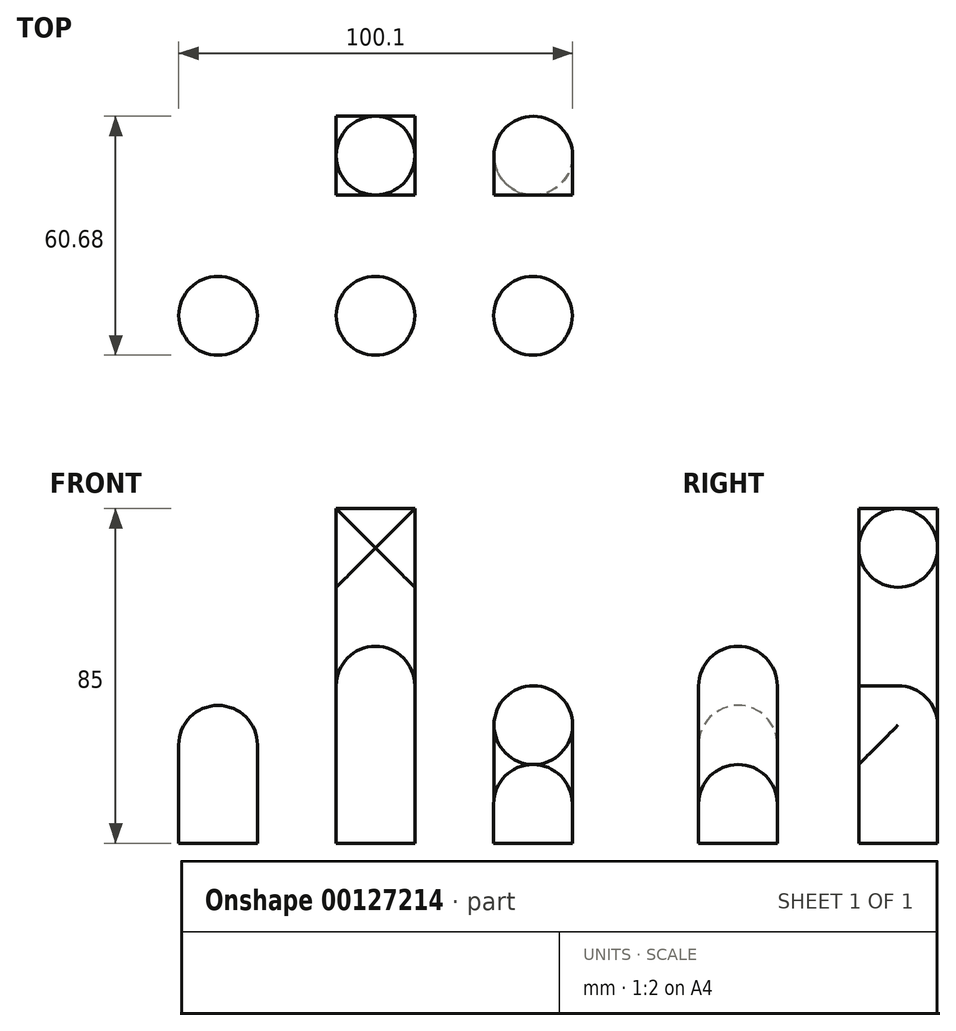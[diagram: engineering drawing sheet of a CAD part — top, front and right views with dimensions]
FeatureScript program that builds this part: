
annotation { "Feature Type Name" : "Feature", "Feature Type Description" : "" }
export const myFeature = defineFeature(function(context is Context, id is Id, definition is map)
    precondition{}
    {
        {
            var Q0;
            Q0=qCreatedBy(makeId("Top.planeOp"),FACE);
            var sketch = newSketch(context, id + "F0", { "sketchPlane" : qUnion([Q0])});
            skCircle(sketch, "E0", {"center": v(0, 0) * mm, "radius": 10 * mm});
            skSolve(sketch);
        }
        {
            var Q0;
            Q0=makeQuery(id+"F0.imprint","IMPRINT",FACE,{"disambiguationData":[TD([[makeQuery(id+"F0.imprint","IMPRINT",EDGE,{"derivedFrom":sQuery(id+"F0.wireOp",EDGE,"E0")}),1.0]])]});
            extrude(context, id + "F1", {"entities" : qUnion([Q0]), "depth" : 85 * mm});
        }
        {
            var Q0;
            Q0=qCreatedBy(makeId("Right.planeOp"),FACE);
            var sketch = newSketch(context, id + "F2", { "sketchPlane" : qUnion([Q0])});
            skLineSegment(sketch, "E1.bottom", {"start": v(-10, 85) * mm, "end": v(10, 85) * mm, "construction": true});
            skLineSegment(sketch, "E1.top", {"start": v(-10, 65) * mm, "end": v(10, 65) * mm, "construction": true});
            skLineSegment(sketch, "E1.left", {"start": v(-10, 85) * mm, "end": v(-10, 65) * mm, "construction": true});
            skLineSegment(sketch, "E1.right", {"start": v(10, 85) * mm, "end": v(10, 65) * mm, "construction": true});
            skLineSegment(sketch, "E2", {"start": v(-10, 0) * mm, "end": v(-10, 65) * mm});
            skLineSegment(sketch, "E3", {"start": v(-10, 65) * mm, "end": v(10, 85) * mm, "construction": true});
            skLineSegment(sketch, "E4", {"start": v(-10, 85) * mm, "end": v(10, 65) * mm, "construction": true});
            skCircle(sketch, "E5", {"center": v(0, 75) * mm, "radius": 10 * mm});
            skSolve(sketch);
        }
        {
            var Q0;
            Q0=makeQuery(id+"F2.imprint","IMPRINT",FACE,{"disambiguationData":[TD([[makeQuery(id+"F2.imprint","IMPRINT",EDGE,{"derivedFrom":sQuery(id+"F2.wireOp",EDGE,"E5")}),1.0]])]});
            extrude(context, id + "F3", {"entities" : qUnion([Q0]), "operationType" : NewBodyOperationType.ADD, "depth" : 10 * mm, "hasSecondDirection" : true, "secondDirectionOppositeDirection" : true, "secondDirectionDepth" : 10 * mm});
        }
        {
            var Q0;
            Q0=qCreatedBy(makeId("Top.planeOp"),FACE);
            var sketch = newSketch(context, id + "F4", { "sketchPlane" : qUnion([Q0])});
            skCircle(sketch, "E6", {"center": v(40.1, 0) * mm, "radius": 10 * mm});
            skSolve(sketch);
        }
        {
            var Q0;
            Q0 = qSketchRegion(id + "F4", true);
            extrude(context, id + "F5", {"entities" : qUnion([Q0]), "depth" : 30 * mm});
        }
        {
            var Q0;
            Q0=qCreatedBy(makeId("Front.planeOp"),FACE);
            var sketch = newSketch(context, id + "F6", { "sketchPlane" : qUnion([Q0])});
            skLineSegment(sketch, "E7", {"start": v(50.1, 30) * mm, "end": v(50.1, 0) * mm, "construction": true});
            skLineSegment(sketch, "E8", {"start": v(50.1, 30) * mm, "end": v(40.1, 30) * mm, "construction": true});
            skCircle(sketch, "E9", {"center": v(40.1, 30) * mm, "radius": 10 * mm});
            skSolve(sketch);
        }
        {
            var Q0;
            Q0=makeQuery(id+"F6.imprint","IMPRINT",FACE,{"disambiguationData":[TD([[makeQuery(id+"F6.imprint","IMPRINT",EDGE,{"derivedFrom":sQuery(id+"F6.wireOp",EDGE,"E9")}),1.0]])]});
            extrude(context, id + "F7", {"entities" : qUnion([Q0]), "operationType" : NewBodyOperationType.ADD, "depth" : 10 * mm});
        }
        {
            var Q0;
            Q0=makeQuery(id+"F5.opExtrude","CAP_FACE",FACE,{"disambiguationData":[OSD([sQuery(id+"F4.wireOp",EDGE,"E6")])],"isStart":false});
            var sketch = newSketch(context, id + "F8", { "sketchPlane" : qUnion([Q0])});
            skArc(sketch, "E10.0", {"start": v(50.1, 0) * mm, "mid": v(40.1, 10) * mm, "end": v(30.1, 0) * mm});
            skLineSegment(sketch, "E11.0", {"start": v(30.1, 0) * mm, "end": v(50.1, 0) * mm, "construction": true});
            skSolve(sketch);
        }
        {
            var Q0;
            Q0=makeQuery(id+"F8.imprint","IMPRINT",FACE,{"disambiguationData":[TD([[makeQuery(id+"F8.imprint","IMPRINT",EDGE,{"derivedFrom":sQuery(id+"F8.wireOp",EDGE,"E10.0")}),1.0]])]});
            var Q1;
            Q1=sQuery(id+"F8.wireOp",EDGE,"E10.0");
            var Q2;
            Q2=sQuery(id+"F8.wireOp",EDGE,"E11.0");
            revolve(context, id + "F9", {"operationType" : NewBodyOperationType.ADD, "entities" : qUnion([Q0]), "surfaceEntities" : qUnion([Q1]), "axis" : qUnion([Q2]), "revolveType" : RevolveType.ONE_DIRECTION, "angle" : 90 * degree});
        }
        {
            var Q0;
            Q0=qCreatedBy(makeId("Top.planeOp"),FACE);
            var sketch = newSketch(context, id + "F10", { "sketchPlane" : qUnion([Q0])});
            skCircle(sketch, "E12", {"center": v(0, -40.68) * mm, "radius": 10 * mm});
            skLineSegment(sketch, "E13", {"start": v(0, -40.68) * mm, "end": v(40, -40.68) * mm, "construction": true});
            skLineSegment(sketch, "E14", {"start": v(0, -40.68) * mm, "end": v(-40, -40.68) * mm, "construction": true});
            skCircle(sketch, "E15", {"center": v(40, -40.68) * mm, "radius": 10 * mm});
            skCircle(sketch, "E16", {"center": v(-40, -40.68) * mm, "radius": 10 * mm});
            skSolve(sketch);
        }
        {
            var Q0;
            Q0=makeQuery(id+"F10.imprint","IMPRINT",FACE,{"disambiguationData":[TD([[makeQuery(id+"F10.imprint","IMPRINT",EDGE,{"derivedFrom":sQuery(id+"F10.wireOp",EDGE,"E12")}),1.0]])]});
            extrude(context, id + "F11", {"entities" : qUnion([Q0]), "depth" : 40 * mm});
        }
        {
            var Q0;
            Q0=makeQuery(id+"F10.imprint","IMPRINT",FACE,{"disambiguationData":[TD([[makeQuery(id+"F10.imprint","IMPRINT",EDGE,{"derivedFrom":sQuery(id+"F10.wireOp",EDGE,"E16")}),1.0]])]});
            extrude(context, id + "F12", {"entities" : qUnion([Q0]), "depth" : 25 * mm});
        }
        {
            var Q0;
            Q0=makeQuery(id+"F10.imprint","IMPRINT",FACE,{"disambiguationData":[TD([[makeQuery(id+"F10.imprint","IMPRINT",EDGE,{"derivedFrom":sQuery(id+"F10.wireOp",EDGE,"E15")}),1.0]])]});
            extrude(context, id + "F13", {"entities" : qUnion([Q0]), "depth" : 10 * mm});
        }
        {
            var Q0;
            Q0=makeQuery(id+"F11.opExtrude","CAP_FACE",FACE,{"disambiguationData":[OSD([sQuery(id+"F10.wireOp",EDGE,"E12")])],"isStart":false});
            var sketch = newSketch(context, id + "F14", { "sketchPlane" : qUnion([Q0])});
            skCircle(sketch, "E17.0", {"center": v(0, -40.68) * mm, "radius": 10 * mm});
            skLineSegment(sketch, "E18", {"start": v(0, -30.68) * mm, "end": v(0, -50.68) * mm});
            skSolve(sketch);
        }
        {
            var Q0;
            {var subQ0=sQuery(id+"F14.wireOp",EDGE,"E18");Q0=makeQuery(id+"F14.imprint","IMPRINT",FACE,{"disambiguationData":[TD([[makeQuery(id+"F14.imprint","IMPRINT",EDGE,{"derivedFrom":subQ0}),1.0]])]});}
            var Q1;
            Q1=sQuery(id+"F14.wireOp",EDGE,"E18");
            revolve(context, id + "F15", {"operationType" : NewBodyOperationType.ADD, "entities" : qUnion([Q0]), "axis" : qUnion([Q1]), "revolveType" : RevolveType.FULL});
        }
        {
            var Q0;
            Q0=makeQuery(id+"F12.opExtrude","CAP_FACE",FACE,{"disambiguationData":[OSD([sQuery(id+"F10.wireOp",EDGE,"E16")])],"isStart":false});
            var sketch = newSketch(context, id + "F16", { "sketchPlane" : qUnion([Q0])});
            skCircle(sketch, "E19.0", {"center": v(-40, -40.68) * mm, "radius": 10 * mm});
            skLineSegment(sketch, "E20", {"start": v(-40, -30.68) * mm, "end": v(-40, -50.68) * mm});
            skSolve(sketch);
        }
        {
            var Q0;
            {var subQ0=sQuery(id+"F16.wireOp",EDGE,"E20");Q0=makeQuery(id+"F16.imprint","IMPRINT",FACE,{"disambiguationData":[TD([[makeQuery(id+"F16.imprint","IMPRINT",EDGE,{"derivedFrom":subQ0}),1.0]])]});}
            var Q1;
            Q1=sQuery(id+"F16.wireOp",EDGE,"E20");
            revolve(context, id + "F17", {"operationType" : NewBodyOperationType.ADD, "entities" : qUnion([Q0]), "axis" : qUnion([Q1]), "revolveType" : RevolveType.FULL});
        }
        {
            var Q0;
            Q0=makeQuery(id+"F13.opExtrude","CAP_FACE",FACE,{"disambiguationData":[OSD([sQuery(id+"F10.wireOp",EDGE,"E15")])],"isStart":false});
            var sketch = newSketch(context, id + "F18", { "sketchPlane" : qUnion([Q0])});
            skCircle(sketch, "E21.0", {"center": v(40, -40.68) * mm, "radius": 10 * mm});
            skLineSegment(sketch, "E22", {"start": v(40, -30.68) * mm, "end": v(40, -50.68) * mm});
            skSolve(sketch);
        }
        {
            var Q0;
            {var subQ0=sQuery(id+"F18.wireOp",EDGE,"E22");Q0=makeQuery(id+"F18.imprint","IMPRINT",FACE,{"disambiguationData":[TD([[makeQuery(id+"F18.imprint","IMPRINT",EDGE,{"derivedFrom":subQ0}),1.0]])]});}
            var Q1;
            Q1=sQuery(id+"F18.wireOp",EDGE,"E22");
            revolve(context, id + "F19", {"operationType" : NewBodyOperationType.ADD, "entities" : qUnion([Q0]), "axis" : qUnion([Q1]), "revolveType" : RevolveType.FULL});
        }
    });
